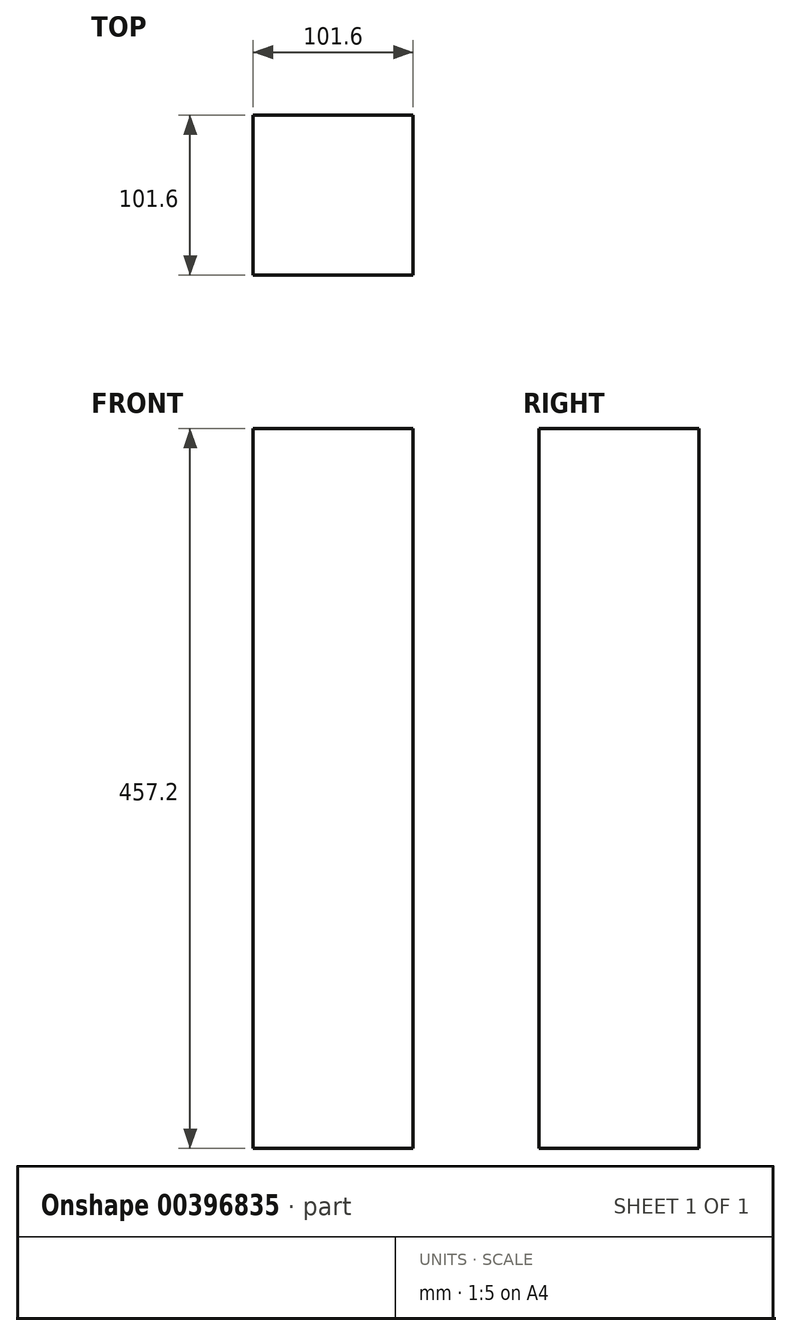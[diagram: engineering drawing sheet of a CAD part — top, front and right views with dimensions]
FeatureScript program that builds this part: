
annotation { "Feature Type Name" : "Feature", "Feature Type Description" : "" }
export const myFeature = defineFeature(function(context is Context, id is Id, definition is map)
    precondition{}
    {
        {
            var Q0;
            Q0=qCreatedBy(makeId("Top.planeOp"),FACE);
            var sketch = newSketch(context, id + "F0", { "sketchPlane" : qUnion([Q0])});
            skLineSegment(sketch, "E0.bottom", {"start": v(-50.8, 50.8) * mm, "end": v(50.8, 50.8) * mm});
            skLineSegment(sketch, "E0.top", {"start": v(-50.8, -50.8) * mm, "end": v(50.8, -50.8) * mm});
            skLineSegment(sketch, "E0.left", {"start": v(-50.8, 50.8) * mm, "end": v(-50.8, -50.8) * mm});
            skLineSegment(sketch, "E0.right", {"start": v(50.8, 50.8) * mm, "end": v(50.8, -50.8) * mm});
            skPoint(sketch, "E0.middle", {"position": v(0, 0) * mm});
            skSolve(sketch);
        }
        {
            var Q0;
            Q0=makeQuery(id+"F0.imprint","IMPRINT",FACE,{"disambiguationData":[TD([[makeQuery(id+"F0.imprint","IMPRINT",EDGE,{"derivedFrom":sQuery(id+"F0.wireOp",EDGE,"E0.bottom")}),-1.0]])]});
            extrude(context, id + "F1", {"entities" : qUnion([Q0]), "depth" : 457.2 * mm});
        }
    });
